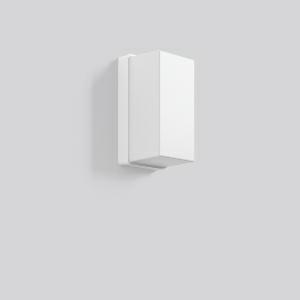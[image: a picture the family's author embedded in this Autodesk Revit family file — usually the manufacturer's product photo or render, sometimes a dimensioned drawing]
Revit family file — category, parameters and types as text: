
# Revit family: rechteck_221170_002_1_6bd5
name_source: partatom
category: Lighting Fixtures
units: mm (PartAtom-declared; Revit-internal decimal feet)

## family parameters
Cut with Voids When Loaded = No
Host = Face
Light Source = No
Part Type = Normal
Room Calculation Point = No
Round Connector Dimension = Use Diameter
Shared = No

## types (1)
- RECHTECK (1 x LED Modul 840, 900 lm, 4000)
    Apparent Load = 9 VA
    CIE Flux Codes = 30 58 82 69 100
    Color Rendering = 80
    Color Temperature = 4000
    Default Elevation = 1800 mm
    Description = Series: RECHTECK
Rectangular surface-mounted luminaire in classic design. Base: plastic. Diffuser: plastic (polypropylene), opal, satin finish. Diffuser fastening: spring system. Suitable for Wall (surface). 
Colour: white
Length: 215 mm
Width: 115 mm
Height: 110 mm
Lamp: LED
Socket: without socket
Colour temperature: 4000K
Colour rendering index (CRI): 80
System power: 9 W
Rated luminous flux: 900 lm
Luminous efficiency: 100 lm/W
Control gear: Regulated power supply
Protection class: I
Type of protection: IP 44
    Height = 110 mm
    Lamp = 1 x LED Modul 840
    Lamp Light Flux = 900 lm
    Lamp count = 1
    Length = 215 mm
    Lifetime = 50000 h
    Luminous efficacy = 100 lm/W
    Manufacturer = RZB
    ModVariant = No
    Model = 221170.002.1
    Mounting Place = Ceiling, Wall
    Mounting Type = Surface mounted
    Number of Poles = 1
    OnlyDefault = Yes
    Power Factor = 1
    Product Name = RECHTECK
    Product group = Surface mounted ceiling and wall luminaires
    ProductGroupID = 305
    Protection Class = Protection class I
    Protection Degree = IP 44
    RLX_Detail_Level = 1
    RLX_Emergency_Light_Flux = 0 lm
    RLX_Emergency_Type = 0
    RLX_Emergency_Type_DB = No
    RlxData = <blob elided: 42613 chars, md5=282ace1d>
    Socket = socket
    Standby Power = 0 W
    System Light Flux = 900 lm
    System Power = 9 W
    Type Comments = Product without accessories
    Type Image = 22144.002.jpg
    URL = http://relux.com
    VarID = ---
    Voltage = 230 V
    Voltage Range = 220-240 V
    Weight = 0.00 kg
    Width = 115 mm

## geometry (parser evidence)
native form markers: Blend x4, Sweep x14
no freeform markers — native parametric forms only
